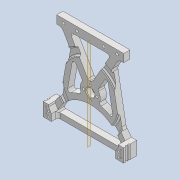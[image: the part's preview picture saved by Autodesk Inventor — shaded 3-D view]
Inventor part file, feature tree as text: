
AUTODESK INVENTOR PART (.ipt)
format: ipt  version: 2020 (Build 240168000, 168)  size: 670,720 bytes
history: native  units: mm
features: sketch x13, extrude x13, projected_geometry x12, fillet x6, mirror x4, thicken_offset x4, reference x4, other x3, plane x2, pattern_circular x1, chamfer x1
ambient origin geometry x8: Origin, YZ Plane, XZ Plane, XY Plane, X Axis, Y Axis, Z Axis, Center Point
bodies: Solid1 (feature_tree)
feature tree (63):
  sketch  "Sketch1"  dims[d0=30.0mm d1=20.0mm]
  plane  "Work Plane1"
  extrude  "Extrusion1"  Depth=20.0mm
  extrude  "Extrusion2"  Depth=4.0mm
  extrude  "Extrusion3"  Depth=10.0mm TaperAngle=0.0deg
  plane  "Work Plane2"
  mirror  "Mirror1"
  extrude  "Extrusion4"  Depth=5.0mm
  extrude  "Extrusion5"  Depth=10.0mm TaperAngle=0.0deg
  extrude  "Extrusion6"  Depth=2.0mm
  fillet  "Fillet1"  Radius=3.5mm
  extrude  "Extrusion7"  Depth=1.5mm
  extrude  "Extrusion8"  Depth=10.0mm
  mirror  "Mirror2"
  fillet  "Fillet2"  Radius=15.0mm
  fillet  "Fillet3"  Radius=3.0mm
  extrude  "Extrusion9"  Depth=4.0mm TaperAngle=0.0deg
  fillet  "Fillet4"  Radius=4.0mm
  thicken_offset  "Thicken1"
  extrude  "Extrusion10"  Depth=1.0mm
  pattern_circular  "Circular Pattern1"  Count=5  [1 undecoded]
  mirror  "Mirror3"
  thicken_offset  "Thicken2"
  thicken_offset  "Thicken3"
  extrude  "Extrusion12"  Depth=5.0mm
  extrude  "Extrusion13"  Depth=1.0mm
  fillet  "Fillet5"  Radius=5.0mm
  fillet  "Fillet6"  Radius=3.0mm
  thicken_offset  "Thicken4"
  chamfer  "Chamfer4"  Distance=4.0mm
  extrude  "Extrusion14"  Depth=1.0mm TaperAngle=0.0deg
  mirror  "Mirror5"
  reference  "Reference1"
  sketch  "Sketch2"  dims[d2=8.0mm d3=4.0mm]
  projected_geometry  "Projected Loop1"
  sketch  "Sketch3"  dims[d4=10.0mm d5=10.0mm d6=0.0mm]
  projected_geometry  "Projected Loop2"
  sketch  "Sketch4"  dims[d7=2.0mm d8=5.0mm]
  projected_geometry  "Projected Loop3"
  projected_geometry  "Projected Loop4"
  sketch  "Sketch5"  dims[d9=30.0deg d10=10.0mm d11=0.0mm]
  projected_geometry  "Projected Loop5"
  sketch  "Sketch6"  dims[d12=2.2mm d13=2.0mm d14=3.5mm]
  projected_geometry  "Projected Loop6"
  sketch  "Sketch7"  dims[d15=1.5mm d16=1.5mm]
  projected_geometry  "Projected Loop7"
  sketch  "Sketch8"  dims[d17=10.0mm d18=0.0mm d19=6.1mm d20=15.0mm d21=3.0mm d22=0.0mm]
  projected_geometry  "Projected Loop8"
  sketch  "Sketch9"  dims[d23=2.5mm d24=4.0mm d25=0.0mm d26=4.0mm]
  reference  "Reference2"
  reference  "Reference3"
  projected_geometry  "Projected Loop9"
  sketch  "Sketch10"  dims[d27=3.0mm d28=0.0mm d29=1.0mm]
  sketch  "Sketch12"  dims[d30=35.0mm]
  projected_geometry  "Projected Loop11"
  sketch  "Sketch13"  dims[d31=6.0mm d32=50.0mm]
  projected_geometry  "Projected Loop12"
  reference  "Reference4"
  sketch  "Sketch14"  dims[d33=20.0mm d34=5.0mm d35=20.0mm d36=5.0mm d37=3.0mm d38=0.0mm d39=4.0mm d40=3.0mm d41=0.0mm d42=1.5mm d43=4.0mm d44=1.5mm d45=1.5mm d46=3.0mm d47=0.0mm d51=2.0mm d52=4.0mm d53=4.0mm d54=5.0mm d55=1.8mm d56=3.0mm d57=0.0mm d58=40.0mm d59=360.0deg d70=1.0mm d71=2.0mm d72=1.0mm d73=2.0mm d74=5.0mm d75=2.0mm d76=5.0mm d77=2.0mm d78=10.0mm d79=2.0mm d80=10.0mm d81=2.0mm d82=9.0mm d83=0.0mm d84=42.0mm d85=53.0mm d86=1.7mm d87=0.0mm d88=1.0mm d89=0.5mm d90=1.7mm d91=1.7mm d95=0.5mm d96=2.0mm d97=45.0deg d98=0.5mm d99=2.0mm d100=2.5mm d101=1.0mm d102=20.0mm d103=0.0mm]
  projected_geometry  "Projected Loop13"
  parser-record x1  (decoder bookkeeping rows leaked as tree rows — omitted from the tree; the rows remain in map.json)
  other  "driver_unit_1.iam"
  other  "driver_wheel_1:1"
note: 1 required parameter value undecoded (feature->parameter linkage not recoverable at this tier; creation-order binding heuristic only, values carry confidence <= 0.55)
note: 1 file-system path scrubbed to <path> (originals preserved in map.json)
